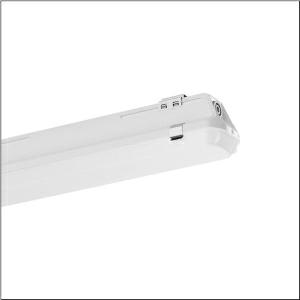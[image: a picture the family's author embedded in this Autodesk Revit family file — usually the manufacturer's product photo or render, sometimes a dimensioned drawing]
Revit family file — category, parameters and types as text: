
# Revit family: monsun_r__11_facade_51ff40mp360h_5056
name_source: partatom
category: Lighting Fixtures
units: mm (PartAtom-declared; Revit-internal decimal feet)

## family parameters
Cut with Voids When Loaded = No
Host = Face
Light Source = No
Part Type = Normal
Room Calculation Point = No
Round Connector Dimension = Use Diameter
Shared = No

## types (1)
- --- (1 x LED, 5790 lm, 33.6 W, 3000K)
    Apparent Load = 34 VA
    CIE Flux Codes = 47 77 93 95 100
    Color Rendering = 80
    Color Temperature = 3000K
    Default Elevation = 1800 mm
    Description = Monsun® 11 facade, damp-proof luminaire, chain hanger, primary optical cover: enclosure, of PMMA, light emission: direct distribution, primary light characteristic: symmetric, installation type: vertical mounting, horizontal mounting, surface-mounted, LED, rated luminous flux: 5.790lm, luminous efficacy: 172lm/W, light colour: 830, colour temperature: 3000K, control gear: ECG, with terminal, 3-pole, max. 2.5mm², mains connection: 220..240V, AC, 50/60Hz, rated input power: 34W, luminaire housing, of glass-fibre reinforced polyester, uncoated, bright grey, with climate membrane, for cables, Ø 8.4..12mm, incl. chain hanger, length: 1.590mm, width: 90mm, height: 88mm, clip for enclosure, of stainless steel (V2A), ceiling mounting element, of stainless steel (V2A), chain hanger, of stainless steel (V2A), protection rating (complete): IP66, insulation class (complete): insulation class I (protective earthing), certification: CE, ENEC, VDE, UKCA, protection symbol: D, impact resistance: IK06, permissible operating ambient temperature: -35..+50°C, standard: EN 60598-2-1, EN 50419, exposed outdoor area, contact your sales advisor before using the luminaires in applications with unclear chemical exposure, large temperature fluctuations or condensation-forming humidity, LABS conformity tested according to VDMA 24364:2018-05, packaging unit: 1 piece
    Height = 89 mm
    Lamp = 1 x LED
    Lamp Light Flux = 5790 lm
    Lamp Power = 33.6 W
    Lamp count = 1
    Length = 1590 mm
    Luminous efficacy = 172 lm/W
    Manufacturer = Siteco
    ModVariant = No
    Model = 51FF40MP360H
    Mounting Place = Ceiling
    Mounting Type = Surface mounted
    Number of Poles = 1
    OnlyDefault = Yes
    Power Factor = 1
    Product Name = Monsun® 11 facade
    Product group = damp-proof luminaire
    ProductGroupID = 300
    Protection Class = Protection class I
    Protection Degree = IP 66
    RLX_Detail_Level = 1
    RLX_Emergency_Light_Flux = 0 lm
    RLX_Emergency_Type = 0
    RLX_Emergency_Type_DB = No
    RlxData = <blob elided: 89693 chars, md5=0a7a8027>
    Socket = socket
    Standby Power = 0 W
    System Light Flux = 5790 lm
    System Power = 34 W
    Type Comments = factory setting: luminous flux: 100 % | (A | C | E) | 77 mA
    Type Image = l_1004748.jpg
    URL = http://relux.com
    VarID = @adj_074663
    Voltage = 0 V
    Weight = 0.00 kg
    Width = 90 mm

## geometry (parser evidence)
native form markers: Blend x4, Sweep x14
no freeform markers — native parametric forms only
